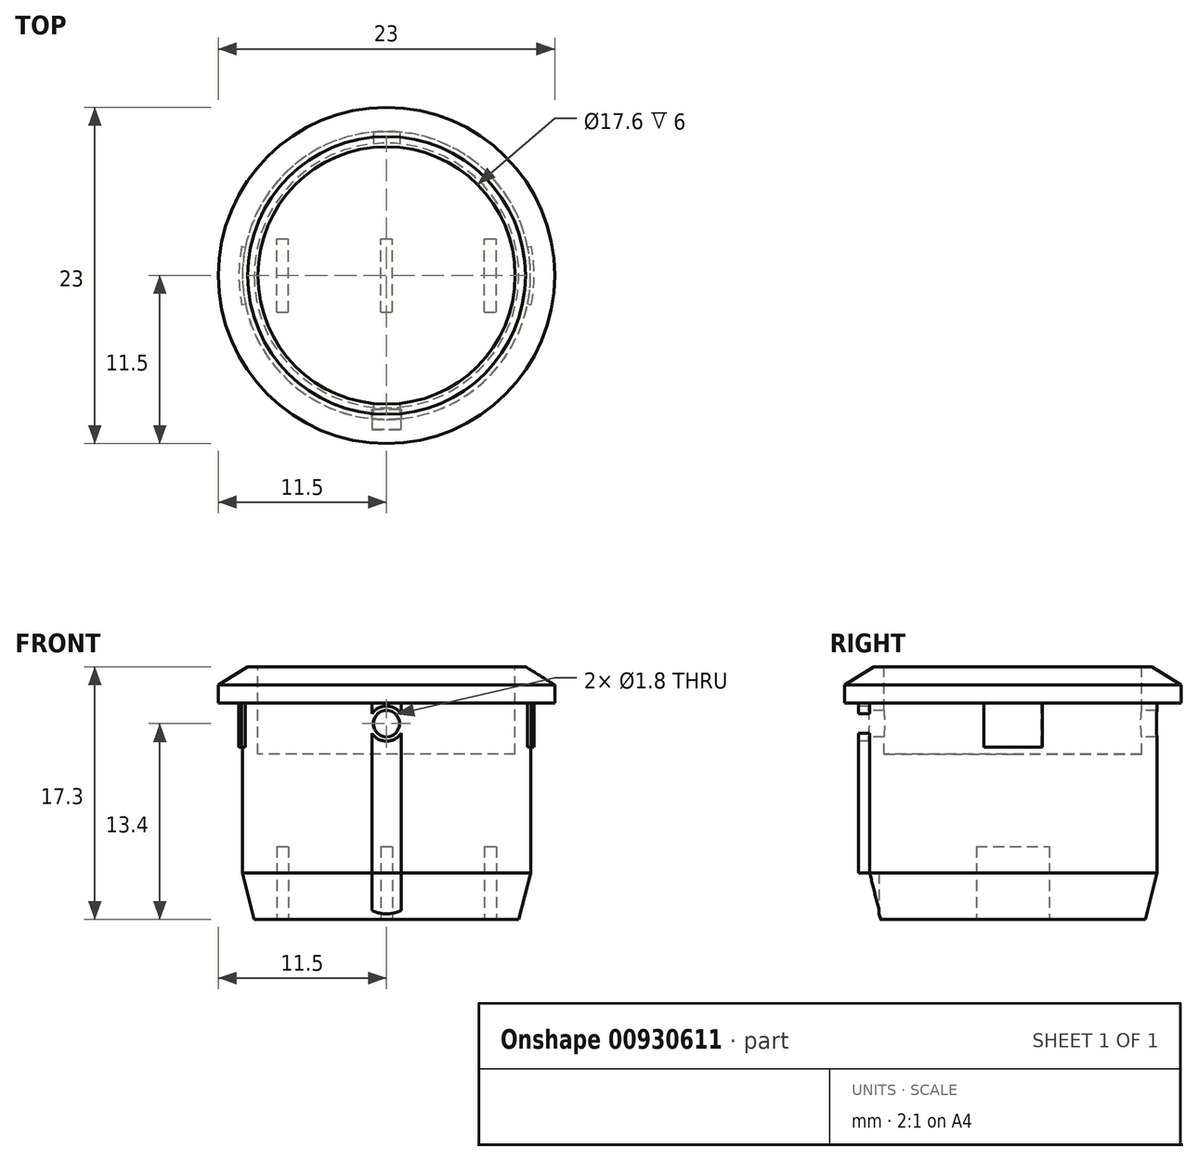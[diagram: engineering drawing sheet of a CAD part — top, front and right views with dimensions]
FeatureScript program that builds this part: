
annotation { "Feature Type Name" : "Feature", "Feature Type Description" : "" }
export const myFeature = defineFeature(function(context is Context, id is Id, definition is map)
    precondition{}
    {
        {
            var Q0;
            Q0=qCreatedBy(makeId("Top.planeOp"),FACE);
            var sketch = newSketch(context, id + "F0", { "sketchPlane" : qUnion([Q0])});
            skCircle(sketch, "E0", {"center": v(0, 0) * mm, "radius": 11.5 * mm});
            skSolve(sketch);
        }
        {
            var Q0;
            Q0=qSketchRegion(id+"F0",true);
            extrude(context, id + "F1", {"entities" : qUnion([Q0]), "depth" : 2.5 * mm, "offsetDistance" : 25 * mm});
        }
        {
            var Q0;
            Q0=makeQuery(id+"F1.opExtrude","CAP_FACE",FACE,{"disambiguationData":[OSD([sQuery(id+"F0.wireOp",EDGE,"E0")])],"isStart":true});
            var sketch = newSketch(context, id + "F2", { "sketchPlane" : qUnion([Q0])});
            skCircle(sketch, "E1", {"center": v(0, 0) * mm, "radius": 9.85 * mm});
            skSolve(sketch);
        }
        {
            var Q0;
            Q0=qSketchRegion(id+"F2",true);
            extrude(context, id + "F3", {"entities" : qUnion([Q0]), "operationType" : NewBodyOperationType.ADD, "depth" : 14.8 * mm, "offsetDistance" : 25 * mm});
        }
        {
            var Q0;
            Q0=makeQuery(id+"F3.opExtrude","CAP_EDGE",EDGE,{"disambiguationData":[OSD([sQuery(id+"F2.wireOp",EDGE,"E1")])],"isStart":false});
            chamfer(context, id + "F4", {"entities" : qUnion([Q0]), "chamferType" : ChamferType.TWO_OFFSETS, "width1" : 0.8 * mm, "oppositeDirection" : false, "width2" : 3.2 * mm, "tangentPropagation" : true});
        }
        {
            var Q0;
            Q0=makeQuery(id+"F1.opExtrude","CAP_EDGE",EDGE,{"disambiguationData":[OSD([sQuery(id+"F0.wireOp",EDGE,"E0")])],"isStart":false});
            chamfer(context, id + "F5", {"entities" : qUnion([Q0]), "chamferType" : ChamferType.TWO_OFFSETS, "width1" : 2 * mm, "oppositeDirection" : false, "width2" : 1.25 * mm, "tangentPropagation" : true});
        }
        {
            var Q0;
            Q0=makeQuery(id+"F1.opExtrude","CAP_FACE",FACE,{"disambiguationData":[OSD([sQuery(id+"F0.wireOp",EDGE,"E0")])],"isStart":false});
            var sketch = newSketch(context, id + "F6", { "sketchPlane" : qUnion([Q0])});
            skCircle(sketch, "E2", {"center": v(0, 0) * mm, "radius": 8.8 * mm});
            skSolve(sketch);
        }
        {
            var Q0;
            Q0=qSketchRegion(id+"F6",true);
            extrude(context, id + "F7", {"entities" : qUnion([Q0]), "operationType" : NewBodyOperationType.REMOVE, "oppositeDirection" : true, "depth" : 6 * mm, "offsetDistance" : 25 * mm});
        }
        {
            var Q0;
            Q0=makeQuery(id+"F3.opExtrude","CAP_FACE",FACE,{"disambiguationData":[OSD([sQuery(id+"F2.wireOp",EDGE,"E1")])],"isStart":false});
            var sketch = newSketch(context, id + "F8", { "sketchPlane" : qUnion([Q0])});
            skLineSegment(sketch, "E3.bottom", {"start": v(-7.5, 2.5) * mm, "end": v(-6.7, 2.5) * mm});
            skLineSegment(sketch, "E3.top", {"start": v(-7.5, -2.5) * mm, "end": v(-6.7, -2.5) * mm});
            skLineSegment(sketch, "E3.left", {"start": v(-7.5, 2.5) * mm, "end": v(-7.5, -2.5) * mm});
            skLineSegment(sketch, "E3.right", {"start": v(-6.7, 2.5) * mm, "end": v(-6.7, -2.5) * mm});
            skLineSegment(sketch, "E4.bottom", {"start": v(-0.4, 2.5) * mm, "end": v(0.4, 2.5) * mm});
            skLineSegment(sketch, "E4.top", {"start": v(-0.4, -2.5) * mm, "end": v(0.4, -2.5) * mm});
            skLineSegment(sketch, "E4.left", {"start": v(-0.4, 2.5) * mm, "end": v(-0.4, -2.5) * mm});
            skLineSegment(sketch, "E4.right", {"start": v(0.4, 2.5) * mm, "end": v(0.4, -2.5) * mm});
            skLineSegment(sketch, "E5.bottom", {"start": v(6.7, 2.5) * mm, "end": v(7.5, 2.5) * mm});
            skLineSegment(sketch, "E5.top", {"start": v(6.7, -2.5) * mm, "end": v(7.5, -2.5) * mm});
            skLineSegment(sketch, "E5.left", {"start": v(6.7, 2.5) * mm, "end": v(6.7, -2.5) * mm});
            skLineSegment(sketch, "E5.right", {"start": v(7.5, 2.5) * mm, "end": v(7.5, -2.5) * mm});
            skSolve(sketch);
        }
        {
            var Q0;
            Q0=qSketchRegion(id+"F8",true);
            extrude(context, id + "F9", {"entities" : qUnion([Q0]), "operationType" : NewBodyOperationType.REMOVE, "oppositeDirection" : true, "depth" : 5 * mm, "offsetDistance" : 25 * mm});
        }
        {
            var Q0;
            Q0=makeQuery(id+"F1.opExtrude","CAP_FACE",FACE,{"disambiguationData":[OSD([sQuery(id+"F0.wireOp",EDGE,"E0")])],"isStart":true});
            var sketch = newSketch(context, id + "F10", { "sketchPlane" : qUnion([Q0])});
            skLineSegment(sketch, "E6", {"start": v(-1, 9.8) * mm, "end": v(-1, 10.55) * mm});
            skLineSegment(sketch, "E7", {"start": v(-1, 10.55) * mm, "end": v(1, 10.55) * mm});
            skLineSegment(sketch, "E8", {"start": v(1, 10.55) * mm, "end": v(1, 9.8) * mm});
            skArc(sketch, "E9", {"start": v(1, 9.8) * mm, "mid": v(0, 9.85) * mm, "end": v(-1, 9.8) * mm});
            skSolve(sketch);
        }
        {
            var Q0;
            Q0=qSketchRegion(id+"F10",true);
            extrude(context, id + "F11", {"entities" : qUnion([Q0]), "operationType" : NewBodyOperationType.ADD, "depth" : 11.6 * mm, "offsetDistance" : 25 * mm});
        }
        {
            var Q0;
            Q0=makeQuery(id+"F3.opExtrude","CAP_FACE",FACE,{"disambiguationData":[OSD([sQuery(id+"F2.wireOp",EDGE,"E1")])],"isStart":false});
            var sketch = newSketch(context, id + "F12", { "sketchPlane" : qUnion([Q0])});
            skLineSegment(sketch, "E10.bottom", {"start": v(-1, 10.55) * mm, "end": v(1, 10.55) * mm});
            skLineSegment(sketch, "E10.top", {"start": v(-1, 9.15) * mm, "end": v(1, 9.15) * mm});
            skLineSegment(sketch, "E10.left", {"start": v(-1, 10.55) * mm, "end": v(-1, 9.15) * mm});
            skLineSegment(sketch, "E10.right", {"start": v(1, 10.55) * mm, "end": v(1, 9.15) * mm});
            skSolve(sketch);
        }
        {
            var Q0;
            Q0=qSketchRegion(id+"F12",true);
            var Q1;
            Q1=makeQuery(id+"F11.opExtrude","CAP_FACE",FACE,{"disambiguationData":[OSD([sQuery(id+"F10.wireOp",EDGE,"E6"),sQuery(id+"F10.wireOp",EDGE,"E7"),sQuery(id+"F10.wireOp",EDGE,"E8"),sQuery(id+"F10.wireOp",EDGE,"E9")])],"isStart":false});
            extrude(context, id + "F13", {"entities" : qUnion([Q0]), "operationType" : NewBodyOperationType.REMOVE, "endBound" : BoundingType.UP_TO_SURFACE, "oppositeDirection" : true, "depth" : 25 * mm, "endBoundEntityFace" : qUnion([Q1]), "offsetDistance" : 25 * mm});
        }
        {
            var Q0;
            Q0=makeQuery(id+"F11.opExtrude","SWEPT_FACE",FACE,{"disambiguationData":[OSD([sQuery(id+"F10.wireOp",EDGE,"E7")])]});
            var sketch = newSketch(context, id + "F14", { "sketchPlane" : qUnion([Q0])});
            skCircle(sketch, "E11", {"center": v(0, -1.4) * mm, "radius": 0.9 * mm});
            skSolve(sketch);
        }
        {
            var Q0;
            Q0=qSketchRegion(id+"F14",true);
            extrude(context, id + "F15", {"entities" : qUnion([Q0]), "operationType" : NewBodyOperationType.REMOVE, "endBound" : BoundingType.THROUGH_ALL, "oppositeDirection" : true, "depth" : 25 * mm, "offsetDistance" : 25 * mm});
        }
        {
            var Q0;
            Q0=makeQuery(id+"F11.opExtrude","SWEPT_FACE",FACE,{"disambiguationData":[OSD([sQuery(id+"F10.wireOp",EDGE,"E7")])]});
            var sketch = newSketch(context, id + "F16", { "sketchPlane" : qUnion([Q0])});
            skCircle(sketch, "E12", {"center": v(0, -1.4) * mm, "radius": 1.2 * mm});
            skSolve(sketch);
        }
        {
            var Q0;
            Q0=qSketchRegion(id+"F16",true);
            var Q1;
            Q1=makeQuery(id+"F3.opExtrude","SWEPT_FACE",FACE,{"disambiguationData":[OSD([sQuery(id+"F2.wireOp",EDGE,"E1")])]});
            extrude(context, id + "F17", {"entities" : qUnion([Q0]), "operationType" : NewBodyOperationType.REMOVE, "endBound" : BoundingType.UP_TO_SURFACE, "oppositeDirection" : true, "depth" : 25 * mm, "endBoundEntityFace" : qUnion([Q1]), "offsetDistance" : 25 * mm});
        }
        {
            var Q0;
            Q0=makeQuery(id+"F1.opExtrude","CAP_FACE",FACE,{"disambiguationData":[OSD([sQuery(id+"F0.wireOp",EDGE,"E0")])],"isStart":true});
            var sketch = newSketch(context, id + "F18", { "sketchPlane" : qUnion([Q0])});
            skLineSegment(sketch, "E13", {"start": v(-9.9, 2) * mm, "end": v(9.9, -2) * mm, "construction": true});
            skLineSegment(sketch, "E14", {"start": v(-9.9, -2) * mm, "end": v(9.9, 2) * mm, "construction": true});
            skArc(sketch, "E15", {"start": v(-9.9, 2) * mm, "mid": v(-10.1, 0) * mm, "end": v(-9.9, -2) * mm});
            skArc(sketch, "E16", {"start": v(9.9, -2) * mm, "mid": v(10.1, 0) * mm, "end": v(9.9, 2) * mm});
            skLineSegment(sketch, "E17", {"start": v(-9.9, 2) * mm, "end": v(-9.9, -2) * mm, "construction": true});
            skArc(sketch, "E18", {"start": v(-9.65, 1.95) * mm, "mid": v(-9.85, 0) * mm, "end": v(-9.65, -1.95) * mm});
            skArc(sketch, "E19", {"start": v(9.65, -1.95) * mm, "mid": v(9.85, 0) * mm, "end": v(9.65, 1.95) * mm});
            skLineSegment(sketch, "E20", {"start": v(-9.9, 2) * mm, "end": v(-9.65, 1.95) * mm});
            skLineSegment(sketch, "E21", {"start": v(-9.9, -2) * mm, "end": v(-9.65, -1.95) * mm});
            skLineSegment(sketch, "E22", {"start": v(9.65, 1.95) * mm, "end": v(9.9, 2) * mm});
            skLineSegment(sketch, "E23", {"start": v(9.65, -1.95) * mm, "end": v(9.9, -2) * mm});
            skSolve(sketch);
        }
        {
            var Q0;
            Q0=qSketchRegion(id+"F18",true);
            extrude(context, id + "F19", {"entities" : qUnion([Q0]), "operationType" : NewBodyOperationType.ADD, "depth" : 3 * mm, "offsetDistance" : 25 * mm});
        }
    });
